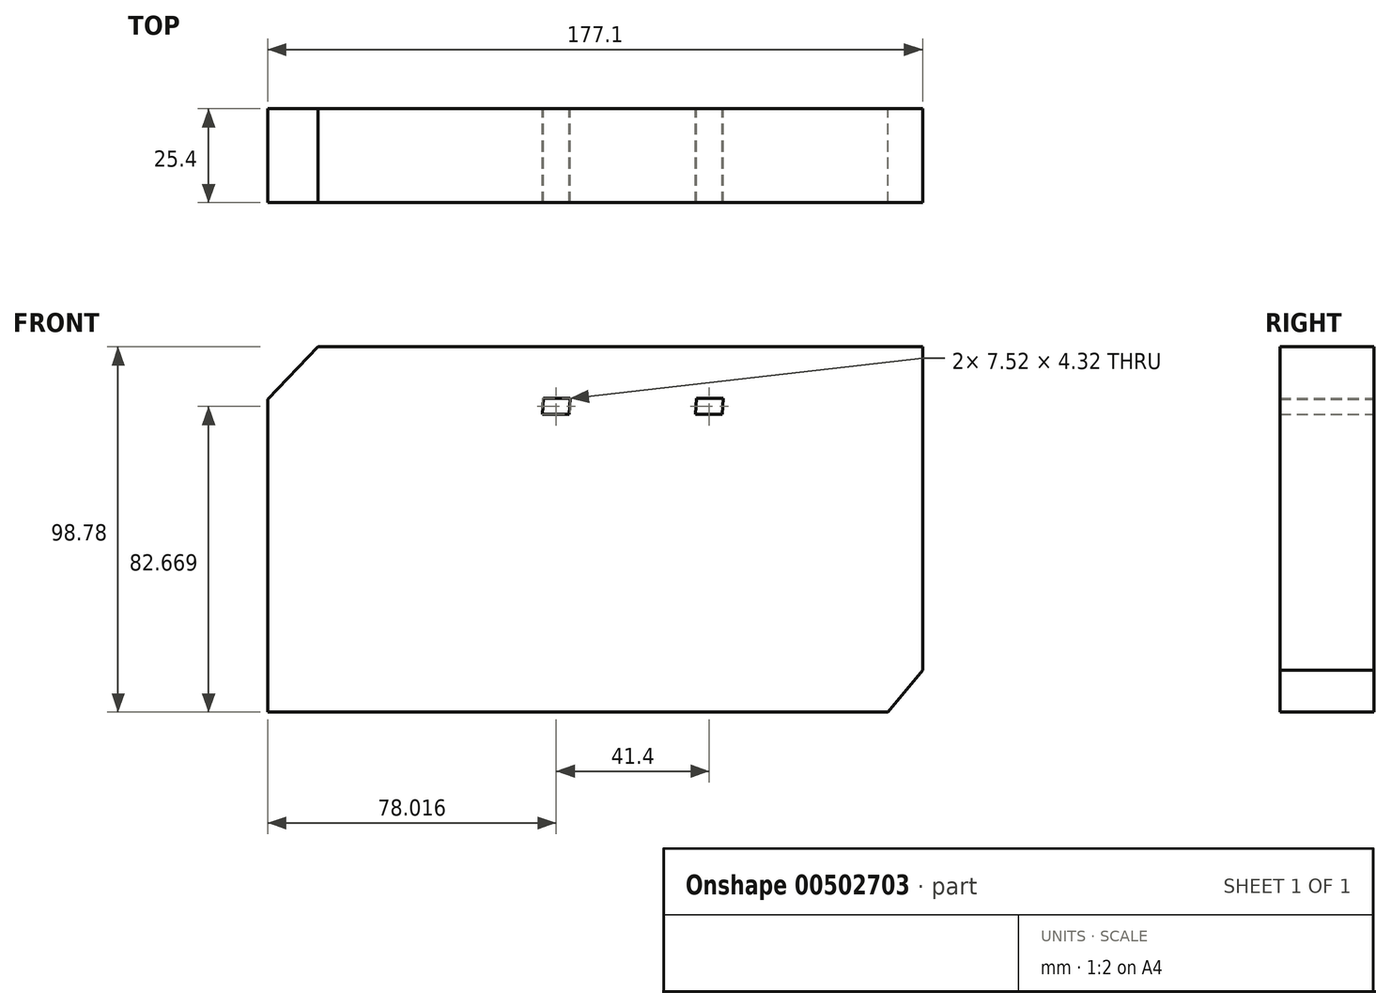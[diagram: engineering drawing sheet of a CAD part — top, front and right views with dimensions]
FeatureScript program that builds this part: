
annotation { "Feature Type Name" : "Feature", "Feature Type Description" : "" }
export const myFeature = defineFeature(function(context is Context, id is Id, definition is map)
    precondition{}
    {
        {
            var Q0;
            Q0=qCreatedBy(makeId("Front.planeOp"),FACE);
            var sketch = newSketch(context, id + "F0", { "sketchPlane" : qUnion([Q0])});
            skLineSegment(sketch, "E0", {"start": v(-74.98, 49.39) * mm, "end": v(-88.55, 35.28) * mm});
            skLineSegment(sketch, "E1", {"start": v(-88.55, 35.28) * mm, "end": v(-88.55, -49.39) * mm});
            skLineSegment(sketch, "E2", {"start": v(-88.55, -49.39) * mm, "end": v(79.18, -49.39) * mm});
            skLineSegment(sketch, "E3", {"start": v(79.18, -49.39) * mm, "end": v(88.55, -38.1) * mm});
            skLineSegment(sketch, "E4", {"start": v(88.55, -38.1) * mm, "end": v(88.55, 49.39) * mm});
            skLineSegment(sketch, "E5", {"start": v(88.55, 49.39) * mm, "end": v(-74.98, 49.39) * mm});
            skLineSegment(sketch, "E6", {"start": v(27.32, 35.44) * mm, "end": v(34.63, 35.44) * mm});
            skLineSegment(sketch, "E7", {"start": v(34.63, 35.44) * mm, "end": v(34.41, 31.12) * mm});
            skLineSegment(sketch, "E8", {"start": v(34.41, 31.12) * mm, "end": v(27.1, 31.12) * mm});
            skLineSegment(sketch, "E9", {"start": v(27.1, 31.12) * mm, "end": v(27.32, 35.44) * mm});
            skLineSegment(sketch, "E10", {"start": v(-14.08, 35.44) * mm, "end": v(-6.77, 35.44) * mm});
            skLineSegment(sketch, "E11", {"start": v(-6.77, 35.44) * mm, "end": v(-6.99, 31.12) * mm});
            skLineSegment(sketch, "E12", {"start": v(-6.99, 31.12) * mm, "end": v(-14.3, 31.12) * mm});
            skLineSegment(sketch, "E13", {"start": v(-14.3, 31.12) * mm, "end": v(-14.08, 35.44) * mm});
            skSolve(sketch);
        }
        {
            var Q0;
            Q0 = qSketchRegion(id + "F0", true);
            extrude(context, id + "F1", {"entities" : qUnion([Q0]), "depth" : 25.4 * mm});
        }
    });
